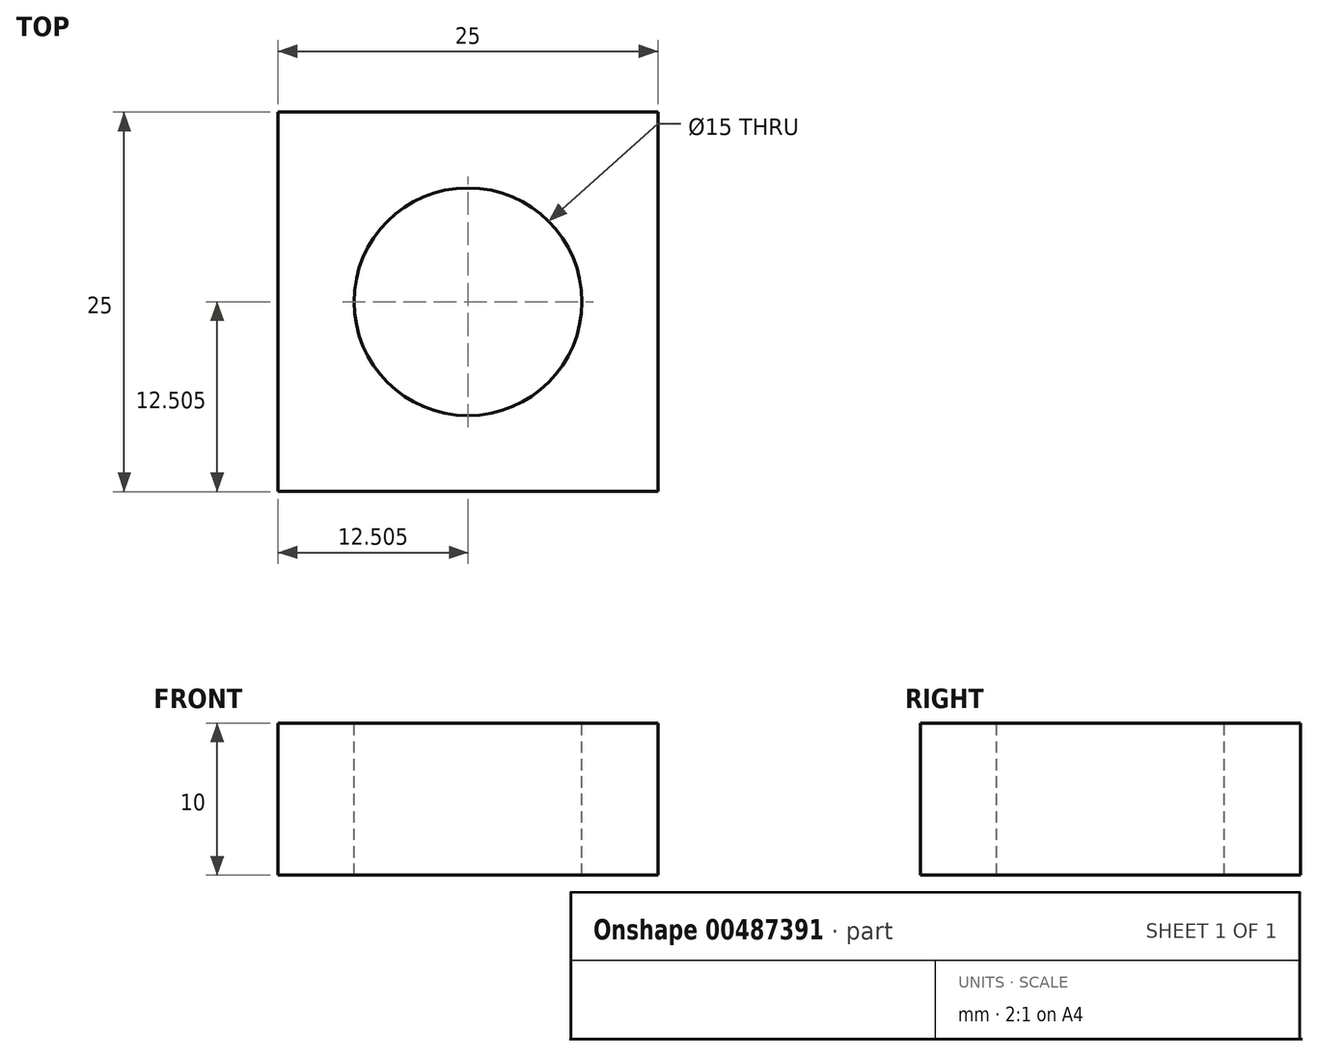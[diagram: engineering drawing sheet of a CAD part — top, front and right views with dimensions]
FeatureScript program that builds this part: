
annotation { "Feature Type Name" : "Feature", "Feature Type Description" : "" }
export const myFeature = defineFeature(function(context is Context, id is Id, definition is map)
    precondition{}
    {
        {
            var Q0;
            Q0=qCreatedBy(makeId("Top.planeOp"),FACE);
            var sketch = newSketch(context, id + "F0", { "sketchPlane" : qUnion([Q0])});
            skLineSegment(sketch, "E0.bottom", {"start": v(-22.39, 23.7) * mm, "end": v(2.61, 23.7) * mm});
            skLineSegment(sketch, "E0.top", {"start": v(-22.39, -1.3) * mm, "end": v(2.61, -1.3) * mm});
            skLineSegment(sketch, "E0.left", {"start": v(-22.39, 23.7) * mm, "end": v(-22.39, -1.3) * mm});
            skLineSegment(sketch, "E0.right", {"start": v(2.61, 23.7) * mm, "end": v(2.61, -1.3) * mm});
            skSolve(sketch);
        }
        {
            var Q0;
            Q0 = qSketchRegion(id + "F0", true);
            extrude(context, id + "F1", {"entities" : qUnion([Q0]), "depth" : 10 * mm});
        }
        {
            var Q0;
            Q0=makeQuery(id+"F1.opExtrude","CAP_FACE",FACE,{"disambiguationData":[OSD([sQuery(id+"F0.wireOp",EDGE,"E0.bottom"),sQuery(id+"F0.wireOp",EDGE,"E0.top"),sQuery(id+"F0.wireOp",EDGE,"E0.left"),sQuery(id+"F0.wireOp",EDGE,"E0.right")])],"isStart":false});
            var sketch = newSketch(context, id + "F2", { "sketchPlane" : qUnion([Q0])});
            skCircle(sketch, "E1", {"center": v(-9.89, 11.2) * mm, "radius": 7.5 * mm});
            skPoint(sketch, "E1.centerSnap0", {"position": v(-22.39, 11.2) * mm});
            skPoint(sketch, "E1.centerSnap1", {"position": v(-9.89, -1.3) * mm});
            skSolve(sketch);
        }
        {
            var Q0;
            Q0=makeQuery(id+"F2.imprint","IMPRINT",FACE,{"disambiguationData":[TD([[makeQuery(id+"F2.imprint","IMPRINT",EDGE,{"derivedFrom":sQuery(id+"F2.wireOp",EDGE,"E1")}),1.0]])]});
            extrude(context, id + "F3", {"entities" : qUnion([Q0]), "operationType" : NewBodyOperationType.REMOVE, "endBound" : BoundingType.THROUGH_ALL, "oppositeDirection" : true, "depth" : 25 * mm});
        }
    });
